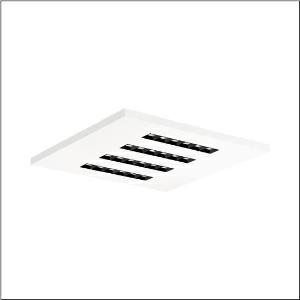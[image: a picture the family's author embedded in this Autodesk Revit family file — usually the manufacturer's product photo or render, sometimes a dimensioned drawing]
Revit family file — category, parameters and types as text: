
# Revit family: silica_21_square_51mx6kds34w
name_source: partatom
category: Lighting Fixtures
units: mm (PartAtom-declared; Revit-internal decimal feet)

## family parameters
Cut with Voids When Loaded = No
Host = Face
Light Source = No
Part Type = Normal
Room Calculation Point = No
Round Connector Dimension = Use Diameter
Shared = No

## types (1)
- --- (1 x LED, 4600 lm, 31.9 W, 3000K)
    Apparent Load = 32 VA
    CIE Flux Codes = 86 100 100 100 100
    Color Rendering = 80
    Color Temperature = 3000K
    Default Elevation = 1800 mm
    Description = Silica 21 Square, office luminaire, primary light control with lens, of PMMA, primary anti-glare with reflector, of PC, black, CAT 2 (L<= 3000cd/m²), light emission: direct distribution, primary light characteristic: symmetric, installation type: lay-in mounting, LED, rated luminous flux: 4.600lm, luminous efficacy: 144lm/W, light colour: 830, colour temperature: 3000K, control gear: DALI 2, with terminal, 5-pole, mains connection: 220..240V, AC, 50/60Hz, rated input power: 31.9W, luminaire housing, of sheet steel, coated, traffic white (RAL 9016), module: M600, length: 597mm, width: 597mm, height: 33mm, protection rating (complete): IP20, insulation class (complete): insulation class I (protective earthing), certification: CE, ENEC, VDE, permissible operating ambient temperature: -20..+40°C, standard: EN 50419, packaging unit: 1 piece
    Height = 0 mm  [stored 0 ft]
    Lamp = 1 x LED
    Lamp Light Flux = 4600 lm
    Lamp Power = 31.9 W
    Lamp count = 1
    Length = 597 mm
    Luminous efficacy = 144 lm/W
    Manufacturer = Siteco
    ModVariant = No
    Model = 51MX6KDS34W
    Mounting Place = Ceiling
    Mounting Type = Recessed
    Number of Poles = 1
    OnlyDefault = Yes
    Power Factor = 1
    Product Name = Silica 21 Square
    Product group = office luminaire | ceiling recessed
    ProductGroupID = 400
    Protection Class = Protection class I
    Protection Degree = IP 20
    RLX_Detail_Level = 1
    RLX_Emergency_Light_Flux = 0 lm
    RLX_Emergency_Type = 0
    RLX_Emergency_Type_DB = No
    RlxData = <blob elided: 21101 chars, md5=ce43b02a>
    Socket = socket
    Standby Power = 0 W
    System Light Flux = 4600 lm
    System Power = 32 W
    Type Comments = factory setting: luminous flux: 100 % | dim-lin: 254 | 430 mA
    Type Image = l_1275207.jpg
    URL = http://relux.com
    VarID = @adj_090677
    Voltage = 0 V
    Weight = 0.00 kg
    Width = 597 mm

note: [stored X ft] marks values corroborated as IEEE doubles in the binary element streams (Revit-internal decimal feet)

## geometry (parser evidence)
native form markers: Blend x4, Sweep x10
no freeform markers — native parametric forms only
